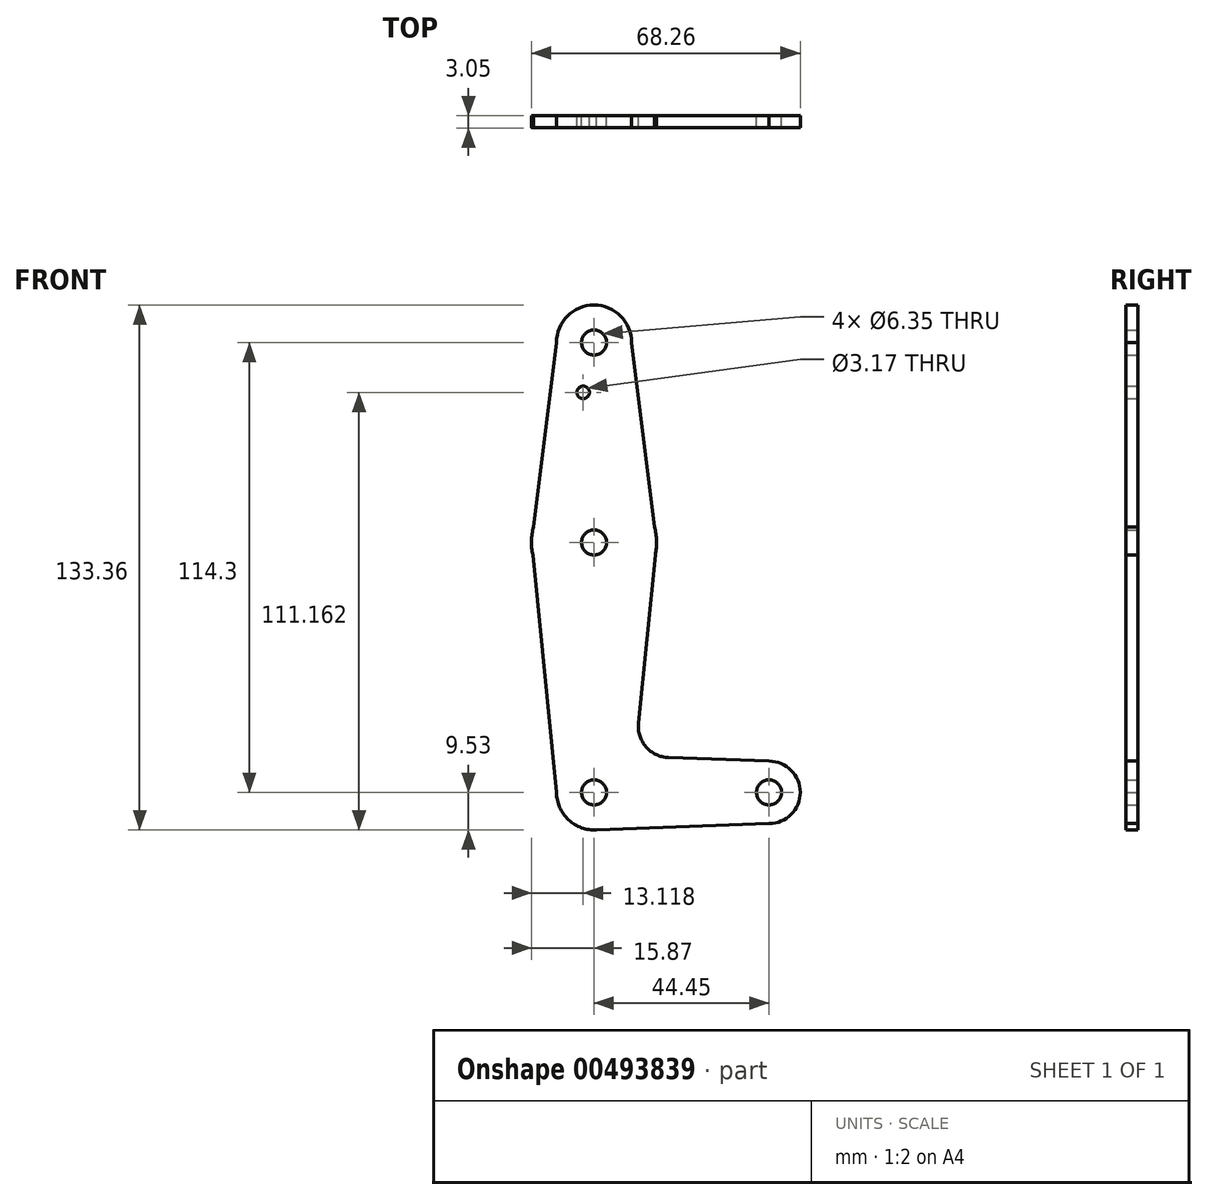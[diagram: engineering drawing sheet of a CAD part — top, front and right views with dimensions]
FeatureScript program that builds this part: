
annotation { "Feature Type Name" : "Feature", "Feature Type Description" : "" }
export const myFeature = defineFeature(function(context is Context, id is Id, definition is map)
    precondition{}
    {
        {
            var Q0;
            Q0=qCreatedBy(makeId("Front.planeOp"),FACE);
            var sketch = newSketch(context, id + "F0", { "sketchPlane" : qUnion([Q0])});
            skLineSegment(sketch, "E0", {"start": v(0, 0) * mm, "end": v(0, 114.3) * mm, "construction": true});
            skLineSegment(sketch, "E1", {"start": v(0, 0) * mm, "end": v(44.45, 0) * mm, "construction": true});
            skCircle(sketch, "E2", {"center": v(0, 0) * mm, "radius": 9.53 * mm});
            skCircle(sketch, "E3", {"center": v(0, 114.3) * mm, "radius": 9.53 * mm});
            skCircle(sketch, "E4", {"center": v(44.45, 0) * mm, "radius": 7.94 * mm});
            skCircle(sketch, "E5", {"center": v(0, 63.5) * mm, "radius": 15.88 * mm});
            skLineSegment(sketch, "E6", {"start": v(-9.52, 114.3) * mm, "end": v(-15.88, 63.5) * mm});
            skLineSegment(sketch, "E7", {"start": v(-15.88, 63.5) * mm, "end": v(-9.52, 0) * mm});
            skLineSegment(sketch, "E8", {"start": v(9.52, 114.3) * mm, "end": v(15.88, 63.5) * mm});
            skLineSegment(sketch, "E9", {"start": v(15.88, 63.5) * mm, "end": v(11.28, 17.59) * mm});
            skLineSegment(sketch, "E10", {"start": v(0, -9.52) * mm, "end": v(44.45, -7.94) * mm});
            skLineSegment(sketch, "E11", {"start": v(18.91, 8.85) * mm, "end": v(44.45, 7.94) * mm});
            skCircle(sketch, "E12", {"center": v(-2.75, 101.63) * mm, "radius": 1.59 * mm});
            skArc(sketch, "E13.filletArc", {"start": v(11.28, 17.59) * mm, "mid": v(13.2, 11.57) * mm, "end": v(18.91, 8.85) * mm});
            skCircle(sketch, "E14", {"center": v(0, 114.3) * mm, "radius": 3.18 * mm});
            skCircle(sketch, "E15", {"center": v(0, 63.5) * mm, "radius": 3.18 * mm});
            skCircle(sketch, "E16", {"center": v(0, 0) * mm, "radius": 3.18 * mm});
            skCircle(sketch, "E17", {"center": v(44.45, 0) * mm, "radius": 3.18 * mm});
            skSolve(sketch);
        }
        {
            var Q0;
            Q0 = qSketchRegion(id + "F0", true);
            extrude(context, id + "F1", {"entities" : qUnion([Q0]), "depth" : 3.05 * mm});
        }
    });
